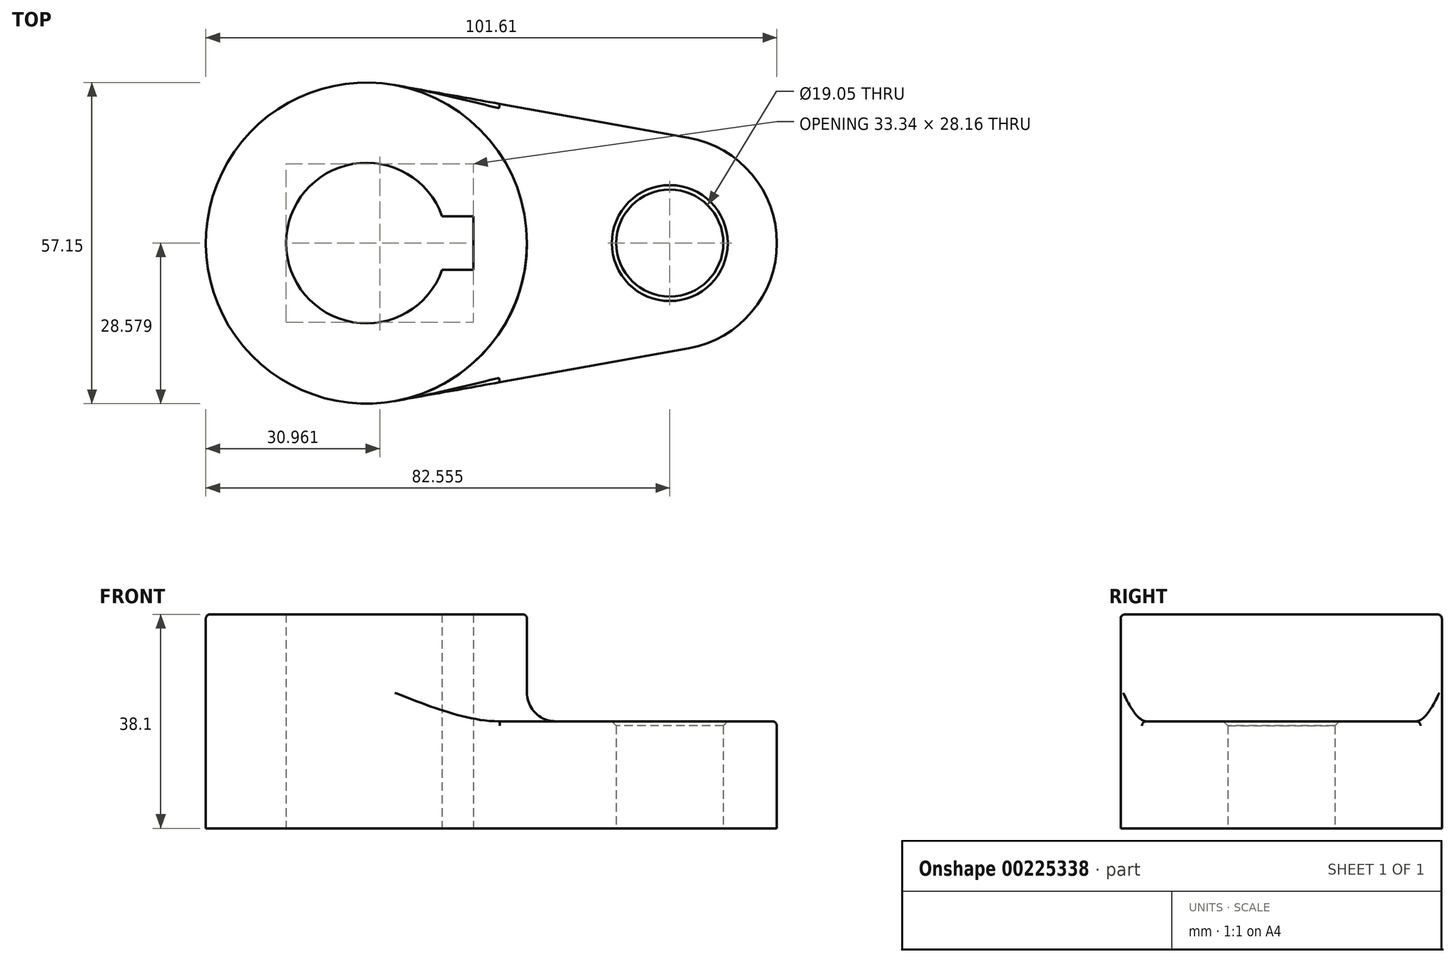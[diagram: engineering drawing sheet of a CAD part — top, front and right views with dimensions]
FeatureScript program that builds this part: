
annotation { "Feature Type Name" : "Feature", "Feature Type Description" : "" }
export const myFeature = defineFeature(function(context is Context, id is Id, definition is map)
    precondition{}
    {
        {
            var Q0;
            Q0=qCreatedBy(makeId("Top.planeOp"),FACE);
            var sketch = newSketch(context, id + "F0", { "sketchPlane" : qUnion([Q0])});
            skCircle(sketch, "E0", {"center": v(34.92, -71.1) * mm, "radius": 19.05 * mm});
            skCircle(sketch, "E1", {"center": v(34.92, -71.1) * mm, "radius": 9.53 * mm});
            skCircle(sketch, "E2", {"center": v(-19.05, -71.1) * mm, "radius": 28.58 * mm});
            skCircle(sketch, "E3", {"center": v(-19.05, -71.1) * mm, "radius": 14.29 * mm});
            skLineSegment(sketch, "E4", {"start": v(-14, -42.97) * mm, "end": v(38.29, -52.35) * mm});
            skLineSegment(sketch, "E5", {"start": v(-14, -99.23) * mm, "end": v(38.29, -89.85) * mm});
            skPoint(sketch, "E6", {"position": v(-47.62, -71.1) * mm});
            skPoint(sketch, "E7", {"position": v(53.97, -71.1) * mm});
            skPoint(sketch, "E8.middle", {"position": v(-4.76, -71.1) * mm});
            skLineSegment(sketch, "E9.bottom", {"start": v(0, -75.86) * mm, "end": v(-38.1, -75.86) * mm});
            skLineSegment(sketch, "E9.top", {"start": v(0, -66.34) * mm, "end": v(-38.1, -66.34) * mm});
            skLineSegment(sketch, "E9.left", {"start": v(0, -75.86) * mm, "end": v(0, -66.34) * mm});
            skLineSegment(sketch, "E9.right", {"start": v(-38.1, -75.86) * mm, "end": v(-38.1, -66.34) * mm});
            skSolve(sketch);
        }
        {
            var Q0;
            Q0 = qSketchRegion(id + "F0", true);
            var Q1;
            {var subQ5=sQuery(id+"F0.wireOp",EDGE,"E9.right");Q1=makeQuery(id+"F0.imprint","IMPRINT",FACE,{"disambiguationData":[TD([[makeQuery(id+"F0.imprint","IMPRINT",EDGE,{"derivedFrom":subQ5}),-1.0]])]});}
            extrude(context, id + "F1", {"entities" : qUnion([Q0, Q1]), "depth" : 19.05 * mm});
        }
        {
            var Q0;
            {var subQ4=sQuery(id+"F0.wireOp",EDGE,"E9.left");Q0=makeQuery(id+"F0.imprint","IMPRINT",FACE,{"disambiguationData":[TD([[makeQuery(id+"F0.imprint","IMPRINT",EDGE,{"derivedFrom":subQ4}),-1.0]])]});}
            var Q1;
            {var subQ5=sQuery(id+"F0.wireOp",EDGE,"E9.right");Q1=makeQuery(id+"F0.imprint","IMPRINT",FACE,{"disambiguationData":[TD([[makeQuery(id+"F0.imprint","IMPRINT",EDGE,{"derivedFrom":subQ5}),-1.0]])]});}
            extrude(context, id + "F2", {"entities" : qUnion([Q0, Q1]), "operationType" : NewBodyOperationType.ADD, "depth" : 38.1 * mm});
        }
        {
            var Q0;
            {var subQ0=sQuery(id+"F0.wireOp",EDGE,"E2");Q0=makeQuery(id+"F2.boolean.opBoolean","INTERSECT",EDGE,{"derivedFrom":[makeQuery(id+"F1.opExtrude","CAP_FACE",FACE,{"disambiguationData":[OSD([sQuery(id+"F0.wireOp",EDGE,"E0"),sQuery(id+"F0.wireOp",EDGE,"E1"),subQ0,sQuery(id+"F0.wireOp",EDGE,"E3"),sQuery(id+"F0.wireOp",EDGE,"E4"),sQuery(id+"F0.wireOp",EDGE,"E5"),sQuery(id+"F0.wireOp",EDGE,"E9.bottom"),sQuery(id+"F0.wireOp",EDGE,"E9.top"),sQuery(id+"F0.wireOp",EDGE,"E9.left")])],"isStart":false}),makeQuery(id+"F2.opExtrude","SWEPT_FACE",FACE,{"disambiguationData":[OSD([subQ0])]})]});}
            fillet(context, id + "F3", {"entities" : qUnion([Q0]), "radius" : 5.08 * mm, "tangentPropagation" : true, "allowEdgeOverflow" : false});
        }
        {
            var Q0;
            Q0=makeQuery(id+"F1.opExtrude","CAP_EDGE",EDGE,{"disambiguationData":[OSD([sQuery(id+"F0.wireOp",EDGE,"E5")])],"isStart":false});
            var Q1;
            Q1=makeQuery(id+"F2.opExtrude","CAP_EDGE",EDGE,{"disambiguationData":[OSD([sQuery(id+"F0.wireOp",EDGE,"E2")])],"isStart":false});
            fillet(context, id + "F4", {"entities" : qUnion([Q0, Q1]), "radius" : 0.79 * mm, "tangentPropagation" : true, "allowEdgeOverflow" : false});
        }
        {
            var Q0;
            Q0=makeQuery(id+"F1.opExtrude","CAP_EDGE",EDGE,{"disambiguationData":[OSD([sQuery(id+"F0.wireOp",EDGE,"E1")])],"isStart":false});
            chamfer(context, id + "F5", {"entities" : qUnion([Q0]), "width" : 0.79 * mm, "tangentPropagation" : true});
        }
    });
